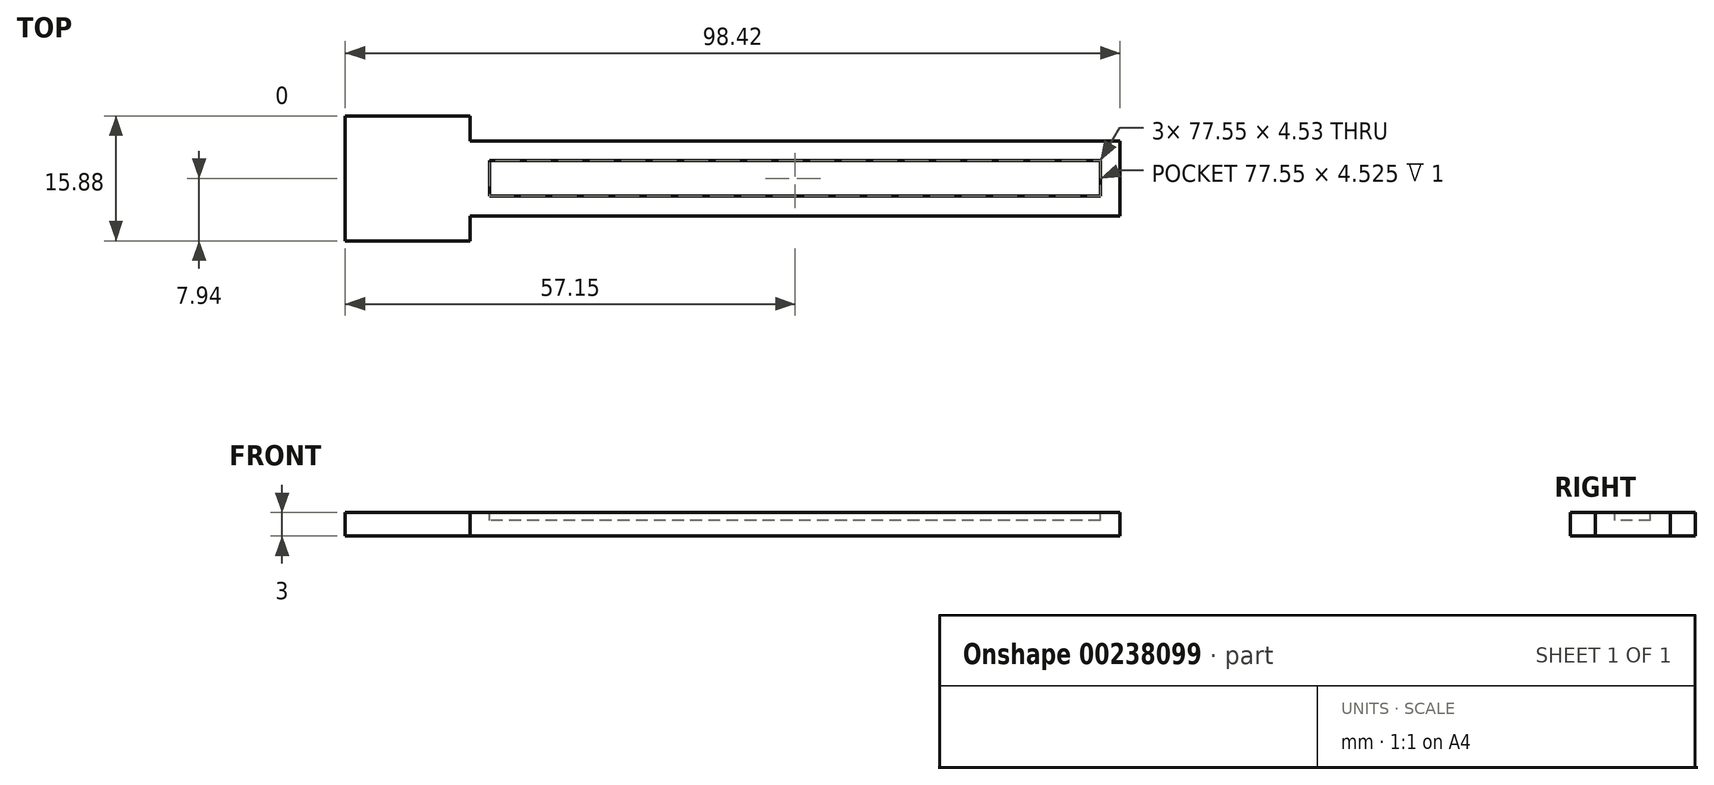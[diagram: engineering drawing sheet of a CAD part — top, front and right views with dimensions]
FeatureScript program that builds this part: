
annotation { "Feature Type Name" : "Feature", "Feature Type Description" : "" }
export const myFeature = defineFeature(function(context is Context, id is Id, definition is map)
    precondition{}
    {
        {
            var Q0;
            Q0=qCreatedBy(makeId("Top.planeOp"),FACE);
            var sketch = newSketch(context, id + "F0", { "sketchPlane" : qUnion([Q0])});
            skLineSegment(sketch, "E0", {"start": v(-57.15, 0) * mm, "end": v(57.15, 0) * mm, "construction": true});
            skLineSegment(sketch, "E1.bottom", {"start": v(41.28, 4.76) * mm, "end": v(-41.28, 4.76) * mm});
            skLineSegment(sketch, "E1.top", {"start": v(41.28, -4.76) * mm, "end": v(-41.28, -4.76) * mm});
            skLineSegment(sketch, "E1.left", {"start": v(41.28, 4.76) * mm, "end": v(41.28, -4.76) * mm});
            skLineSegment(sketch, "E1.right", {"start": v(-41.28, 4.76) * mm, "end": v(-41.28, -4.76) * mm});
            skPoint(sketch, "E1.middle", {"position": v(0, 0) * mm});
            skLineSegment(sketch, "E2.bottom", {"start": v(-41.28, 7.94) * mm, "end": v(-57.15, 7.94) * mm});
            skLineSegment(sketch, "E2.top", {"start": v(-41.28, -7.94) * mm, "end": v(-57.15, -7.94) * mm});
            skLineSegment(sketch, "E2.left", {"start": v(-41.28, 7.94) * mm, "end": v(-41.28, -7.94) * mm});
            skLineSegment(sketch, "E2.right", {"start": v(-57.15, 7.94) * mm, "end": v(-57.15, -7.94) * mm});
            skPoint(sketch, "E2.middle", {"position": v(-49.21, 0) * mm});
            skLineSegment(sketch, "E3.bottom", {"start": v(41.28, 4.76) * mm, "end": v(57.15, 4.76) * mm});
            skLineSegment(sketch, "E3.top", {"start": v(41.28, -4.76) * mm, "end": v(57.15, -4.76) * mm});
            skLineSegment(sketch, "E3.right", {"start": v(57.15, 4.76) * mm, "end": v(57.15, -4.76) * mm});
            skSolve(sketch);
        }
        {
            var Q0;
            {var subQ3=sQuery(id+"F0.wireOp",EDGE,"E2.bottom");Q0=makeQuery(id+"F0.imprint","IMPRINT",FACE,{"disambiguationData":[TD([[makeQuery(id+"F0.imprint","IMPRINT",EDGE,{"derivedFrom":subQ3}),1.0]])]});}
            var Q1;
            {var subQ0=sQuery(id+"F0.wireOp",EDGE,"E1.bottom");Q1=makeQuery(id+"F0.imprint","IMPRINT",FACE,{"disambiguationData":[TD([[makeQuery(id+"F0.imprint","IMPRINT",EDGE,{"derivedFrom":subQ0}),1.0]])]});}
            extrude(context, id + "F1", {"entities" : qUnion([Q0, Q1]), "depth" : 3 * mm});
        }
        {
            var Q0;
            Q0=makeQuery(id+"F1.opExtrude","CAP_FACE",FACE,{"disambiguationData":[OSD([sQuery(id+"F0.wireOp",EDGE,"E1.bottom"),sQuery(id+"F0.wireOp",EDGE,"E1.top"),sQuery(id+"F0.wireOp",EDGE,"E2.bottom"),sQuery(id+"F0.wireOp",EDGE,"E2.top"),sQuery(id+"F0.wireOp",EDGE,"E2.left"),sQuery(id+"F0.wireOp",EDGE,"E2.right"),sQuery(id+"F0.wireOp",EDGE,"E3.bottom"),sQuery(id+"F0.wireOp",EDGE,"E3.top"),sQuery(id+"F0.wireOp",EDGE,"E3.right")])],"isStart":false});
            var sketch = newSketch(context, id + "F2", { "sketchPlane" : qUnion([Q0])});
            skLineSegment(sketch, "E4.bottom", {"start": v(38.78, 2.26) * mm, "end": v(-38.78, 2.26) * mm});
            skLineSegment(sketch, "E4.top", {"start": v(38.78, -2.26) * mm, "end": v(-38.78, -2.26) * mm});
            skLineSegment(sketch, "E4.left", {"start": v(38.78, 2.26) * mm, "end": v(38.78, -2.26) * mm});
            skLineSegment(sketch, "E4.right", {"start": v(-38.78, 2.26) * mm, "end": v(-38.78, -2.26) * mm});
            skSolve(sketch);
        }
        {
            var Q0;
            Q0 = qSketchRegion(id + "F2", true);
            extrude(context, id + "F3", {"entities" : qUnion([Q0]), "operationType" : NewBodyOperationType.REMOVE, "oppositeDirection" : true, "depth" : 1 * mm});
        }
    });
